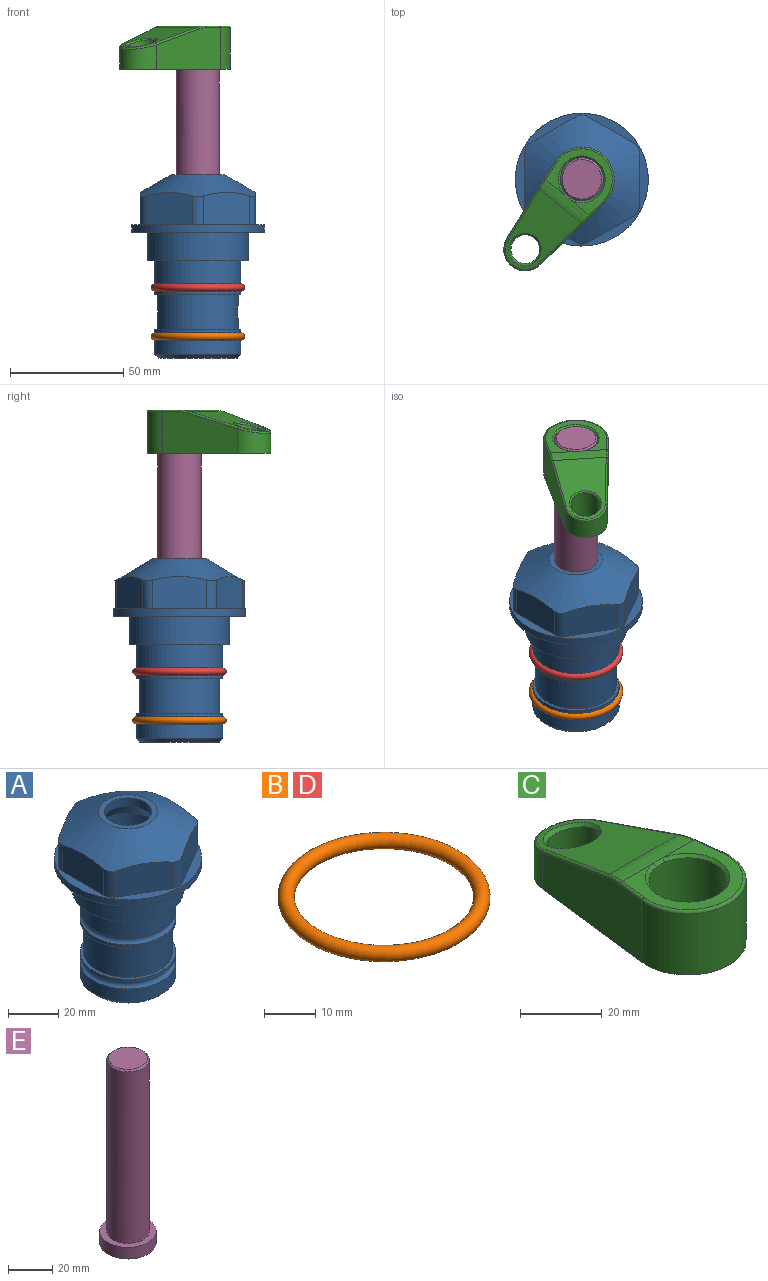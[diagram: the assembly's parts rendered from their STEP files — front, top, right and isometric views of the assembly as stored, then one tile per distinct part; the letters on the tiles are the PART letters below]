
ASSEMBLY  parts=5 mates=4
PART A: 36 faces, bbox 58.7x58.7x81 mm
  f0: cylinder r=17.78mm len=35.56mm, axis (0,0,1), area 1670.8mm2, adj f23,f24,f31
  f1: cylinder r=19.05mm len=38.1mm, axis (0,0,1), area 1191.9mm2, adj f26,f27,f30
  f2: plane 58.66x58.66mm, normal (0,0,-1), area 1150.6mm2, adj f3,f28
  f3: cylinder r=29.33mm len=58.66mm, axis (0,0,-1), area 585.1mm2, adj f2,f4
  f4: plane 58.66x58.66mm, normal (0,0,1), area 475.9mm2, adj f3,f5,f6,f7,f8,f9,f10,f11
  f5: plane 20.32x14.34mm, normal (-0.5,0.87,0), area 324.4mm2, adj f4,f15,f16,f17
  f6: plane 20.32x14.34mm, normal (0.5,0.87,0), area 324.4mm2, adj f4,f14,f15,f17
  f7: plane 23.48x14.34mm, normal (1,0,0), area 324.4mm2, adj f4,f13,f14,f17
  f8: plane 20.32x14.34mm, normal (0.5,-0.87,0), area 324.4mm2, adj f4,f12,f13,f17
  f9: plane 20.32x14.34mm, normal (-0.5,-0.87,0), area 324.4mm2, adj f4,f11,f12,f17
  f10: plane 23.48x14.34mm, normal (-1,0,0), area 324.4mm2, adj f4,f11,f16,f17
  f11: cylinder r=5.08mm len=12.85mm, axis (0,0,-1), area 67.2mm2, adj f4,f9,f10,f17
  f12: cylinder r=5.08mm len=12.85mm, axis (0,0,-1), area 67.2mm2, adj f4,f8,f9,f17
  f13: cylinder r=5.08mm len=12.85mm, axis (0,0,-1), area 67.2mm2, adj f4,f7,f8,f17
  f14: cylinder r=5.08mm len=12.85mm, axis (0,0,-1), area 67.2mm2, adj f4,f6,f7,f17
  f15: cylinder r=5.08mm len=12.85mm, axis (0,0,-1), area 67.2mm2, adj f4,f5,f6,f17
  f16: cylinder r=5.08mm len=12.85mm, axis (0,0,-1), area 67.2mm2, adj f4,f5,f10,f17
  f17: cone r=11.73mm half-angle=60deg, axis (0,0,-1), area 2071.8mm2, adj f5,f6,f7,f8,f9,f10,f11,f12
  f18: plane 23.46x23.46mm, normal (0,0,1), area 147.4mm2, adj f17,f35
  f19: plane 34.93x34.93mm, normal (0,0,-1), area 958mm2, adj f29
  f20: cylinder r=19.05mm len=38.1mm, axis (0,0,1), area 760.1mm2, adj f21,f29
  f21: torus R=19.05mm, axis (0,0,1), area 565.3mm2, adj f20,f22
  f22: cylinder r=19.05mm len=38.1mm, axis (0,0,1), area 190mm2, adj f21,f23
  f23: plane 38.1x38.1mm, normal (0,0,1), area 146.9mm2, adj f0,f22
  f24: plane 38.1x38.1mm, normal (0,0,-1), area 146.9mm2, adj f0,f25
  f25: cylinder r=19.05mm len=38.1mm, axis (0,0,1), area 190mm2, adj f24,f26
  f26: torus R=19.05mm, axis (0,0,1), area 565.3mm2, adj f1,f25
  f27: plane 44.45x44.45mm, normal (0,0,-1), area 411.7mm2, adj f1,f28
  f28: cylinder r=22.23mm len=44.45mm, axis (0,0,1), area 1773.5mm2, adj f2,f27
  f29: cone r=19.05mm half-angle=45deg, axis (0,0,1), area 257.5mm2, adj f19,f20
  f30: cylinder r=3.17mm len=6.75mm, axis (-1,0,0), area 128mm2, adj f1,f33
  f31: cylinder r=3.17mm len=6.35mm, axis (-1,0,0), area 102.5mm2, adj f0,f33
  f32: plane 25.4x25.4mm, normal (0,0,1), area 506.7mm2, adj f33
  f33: cylinder r=12.7mm len=66.42mm, axis (0,0,-1), area 5236.2mm2, adj f30,f31,f32,f34
  f34: cone r=9.53mm half-angle=30deg, axis (0,0,-1), area 443.4mm2, adj f33,f35
  f35: cylinder r=9.53mm len=19.05mm, axis (0,0,-1), area 240.9mm2, adj f18,f34
PART B: 1 faces, bbox 44.7x44.7x3.2 mm
  f0: torus R=19.05mm, axis (0,0,1), area 1193.9mm2
PART C: 31 faces, bbox 31.7x65.5x19.8 mm
  f0: plane 39.12x18.26mm, normal (0.99,0.12,0), area 612.2mm2, adj f1,f4,f7,f11,f13,f15
  f1: cylinder r=9.53mm len=18.91mm, axis (0,0,-1), area 296.1mm2, adj f0,f2,f7,f17
  f2: plane 39.12x18.26mm, normal (-0.99,0.12,0), area 612.2mm2, adj f1,f4,f7,f12,f14,f16
  f3: cylinder r=6.35mm len=12.7mm, axis (0,0,-1), area 362.4mm2, adj f7,f18
  f4: cylinder r=14.29mm len=28.58mm, axis (0,0,-1), area 882.2mm2, adj f0,f2,f7,f10
  f5: cylinder r=9.53mm len=19.05mm, axis (0,0,-1), area 1092.6mm2, adj f7,f19,f20
  f6: plane 26.99x23.69mm, normal (0,0,1), area 216.2mm2, adj f9,f10,f11,f12,f19
  f7: plane 63.5x28.58mm, normal (0,0,-1), area 661.8mm2, adj f0,f1,f2,f3,f4,f5,f22,f23
  f8: plane 33.52x23.6mm, normal (0,0.26,0.97), area 486mm2, adj f9,f15,f16,f17,f18
  f9: cylinder r=19.05mm len=24.72mm, axis (1,0,0), area 120.4mm2, adj f6,f8,f13,f14,f20
  f10: torus R=13.49mm, axis (0,0,1), area 59mm2, adj f4,f6,f11,f12
  f11: cylinder r=0.79mm len=8.67mm, axis (0.12,-0.99,0), area 10.8mm2, adj f0,f6,f10,f13
  f12: cylinder r=0.79mm len=8.67mm, axis (0.12,0.99,0), area 10.8mm2, adj f2,f6,f10,f14
  f13: bspline ~4.95x1.42mm, area 6.1mm2, adj f0,f9,f11,f15
  f14: bspline ~4.95x1.42mm, area 6.1mm2, adj f2,f9,f12,f16
  f15: cylinder r=0.79mm len=25.95mm, axis (0.12,-0.96,0.26), area 32.9mm2, adj f0,f8,f13,f17
  f16: cylinder r=0.79mm len=25.95mm, axis (0.12,0.96,-0.26), area 32.9mm2, adj f2,f8,f14,f17
  f17: bspline ~18.91x8.38mm, area 30mm2, adj f1,f8,f15,f16
  f18: bspline ~14.29x14.29mm, area 48.3mm2, adj f3,f8
  f19: cone r=9.53mm half-angle=45deg, axis (0,0,1), area 66.5mm2, adj f5,f6,f20
  f20: bspline ~3.22x0.96mm, area 3.5mm2, adj f5,f9,f19
  f21: plane 2.75x2.72mm, normal (0,0,-1), area 2.9mm2, adj f23,f25,f28
  f22: plane 23.05x15.88mm, normal (-0.99,-0.12,0), area 323.6mm2, adj f7,f25,f26,f27,f28,f29
  f23: plane 23.05x15.88mm, normal (0.99,-0.12,0), area 323.6mm2, adj f7,f21,f25,f27,f28,f30
  f24: cylinder r=9.53mm len=10.69mm, axis (0,0,-1), area 114.7mm2, adj f7,f27,f29,f30
  f25: cylinder r=12.7mm len=20.59mm, axis (0,0,-1), area 381.1mm2, adj f7,f21,f22,f23,f26,f28
  f26: plane 2.75x2.72mm, normal (0,0,-1), area 2.9mm2, adj f22,f25,f28
  f27: plane 19.72x18.37mm, normal (0,-0.26,-0.97), area 291.8mm2, adj f22,f23,f24,f28,f29,f30
  f28: cylinder r=15.88mm len=19.92mm, axis (1,0,0), area 54.8mm2, adj f21,f22,f23,f25,f26,f27
  f29: cylinder r=1.59mm len=11mm, axis (0,0,-1), area 34.7mm2, adj f7,f22,f24,f27
  f30: cylinder r=1.59mm len=11mm, axis (0,0,-1), area 34.7mm2, adj f7,f23,f24,f27
PART D: same geometry as B
PART E: 6 faces, bbox 25.4x25.4x101.6 mm
  f0: plane 17.46x17.46mm, normal (0,0,1), area 239.5mm2, adj f5
  f1: plane 25.4x25.4mm, normal (0,0,-1), area 506.7mm2, adj f2
  f2: cylinder r=12.7mm len=25.4mm, axis (0,0,1), area 506.7mm2, adj f1,f3
  f3: plane 25.4x25.4mm, normal (0,0,1), area 221.7mm2, adj f2,f4
  f4: cylinder r=9.53mm len=94.46mm, axis (0,0,1), area 5653mm2, adj f3,f5
  f5: cone r=8.73mm half-angle=45deg, axis (0,0,-1), area 64.4mm2, adj f0,f4
PLACE A at identity fixed
PLACE B t=(0,0,-21.59)mm
PLACE C rot(axis=(0,0,1),141deg) t=(0,0,27.55)mm
PLACE D at identity
PLACE E rot(axis=(0,0,1),141deg) t=(0,0,27.55)mm
MATE cylindrical E.f2 <-> A.f0  axis (0,0,-1) through (0,0,-10.55)mm
MATE fastened C.f4 <-> E.f2  axis (0,0,1) through (0,0,91.05)mm
MATE fastened B.f0 <-> A.f0  axis (0,0,1) through (0,0,-46.1)mm
MATE fastened D.f0 <-> A.f0  axis (0,0,1) through (0,0,-24.51)mm
